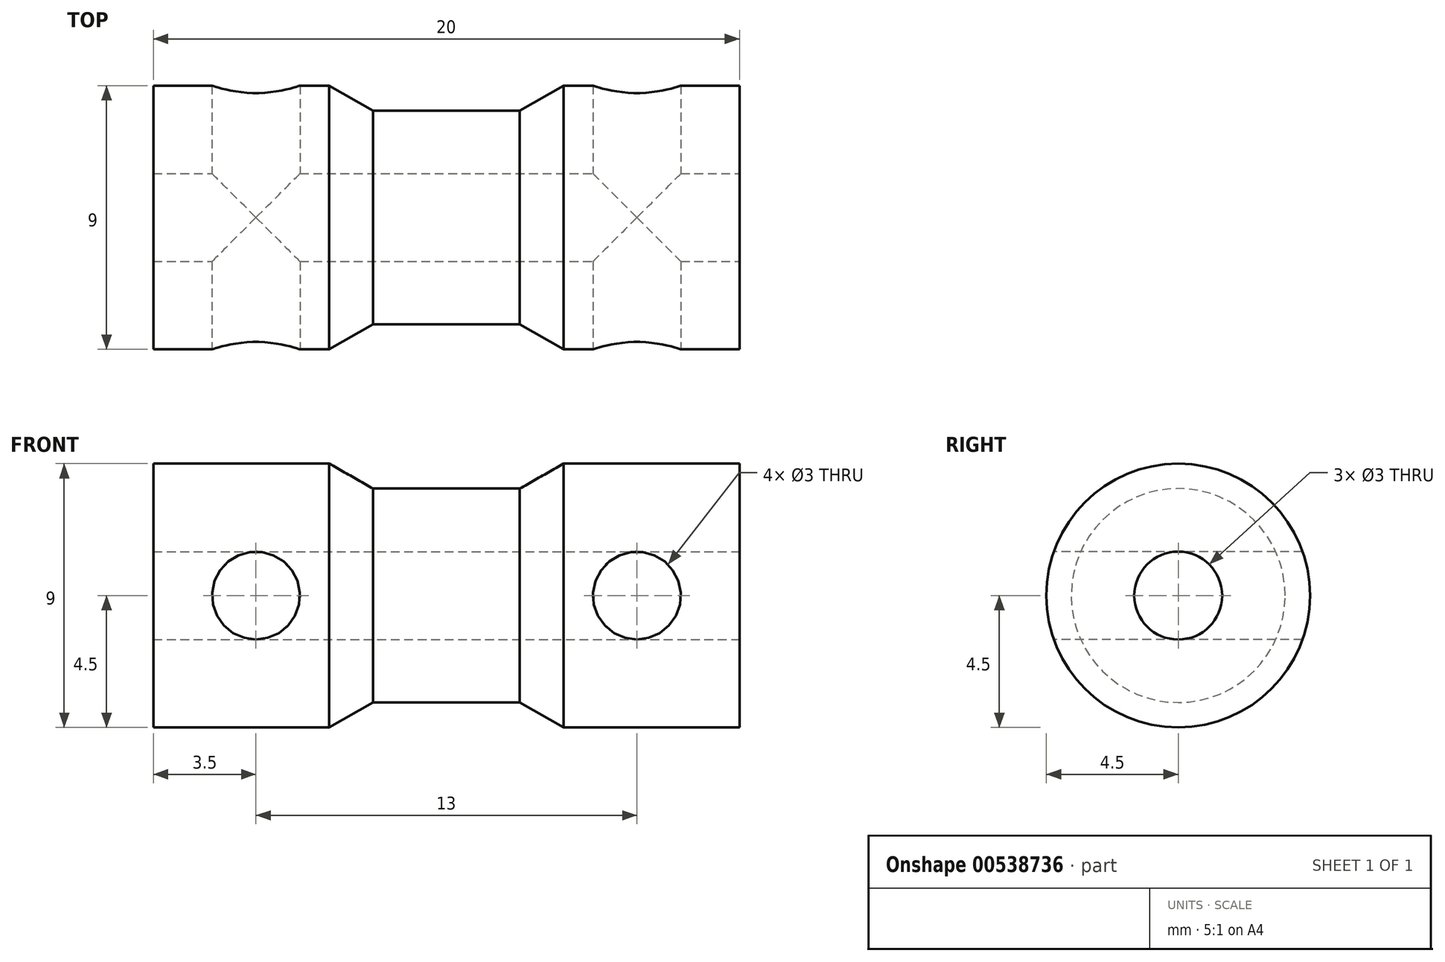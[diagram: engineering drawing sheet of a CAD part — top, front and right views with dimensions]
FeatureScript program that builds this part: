
annotation { "Feature Type Name" : "Feature", "Feature Type Description" : "" }
export const myFeature = defineFeature(function(context is Context, id is Id, definition is map)
    precondition{}
    {
        {
            var Q0;
            Q0=qCreatedBy(makeId("Front.planeOp"),FACE);
            var sketch = newSketch(context, id + "F0", { "sketchPlane" : qUnion([Q0])});
            skLineSegment(sketch, "E0", {"start": v(-10, 0) * mm, "end": v(-10, -4.5) * mm});
            skLineSegment(sketch, "E1", {"start": v(-10, -4.5) * mm, "end": v(-4, -4.5) * mm});
            skLineSegment(sketch, "E2", {"start": v(-2.5, -3.65) * mm, "end": v(0, -3.65) * mm});
            skLineSegment(sketch, "E3", {"start": v(-4, -4.5) * mm, "end": v(-2.5, -3.65) * mm});
            skLineSegment(sketch, "E4.MirrorCS", {"start": v(4, -4.5) * mm, "end": v(2.5, -3.65) * mm});
            skLineSegment(sketch, "E5.MirrorCS", {"start": v(10, -4.5) * mm, "end": v(4, -4.5) * mm});
            skLineSegment(sketch, "E6.MirrorCS", {"start": v(10, 0) * mm, "end": v(10, -4.5) * mm});
            skLineSegment(sketch, "E7.MirrorCS", {"start": v(2.5, -3.65) * mm, "end": v(0, -3.65) * mm});
            skLineSegment(sketch, "E8", {"start": v(-10, 0) * mm, "end": v(10, 0) * mm});
            skSolve(sketch);
        }
        {
            var Q0;
            Q0=makeQuery(id+"F0.imprint","IMPRINT",FACE,{"disambiguationData":[TD([[makeQuery(id+"F0.imprint","IMPRINT",EDGE,{"derivedFrom":sQuery(id+"F0.wireOp",EDGE,"E0")}),1.0]])]});
            var Q1;
            Q1=sQuery(id+"F0.wireOp",EDGE,"E8");
            revolve(context, id + "F1", {"surfaceOperationType" : NewSurfaceOperationType.NEW, "entities" : qUnion([Q0]), "axis" : qUnion([Q1]), "revolveType" : RevolveType.FULL});
        }
        {
            var Q0;
            Q0=qCreatedBy(makeId("Front.planeOp"),FACE);
            var sketch = newSketch(context, id + "F2", { "sketchPlane" : qUnion([Q0])});
            skCircle(sketch, "E9", {"center": v(-6.5, 0) * mm, "radius": 1.5 * mm});
            skCircle(sketch, "E10.MirrorC", {"center": v(6.5, 0) * mm, "radius": 1.5 * mm});
            skSolve(sketch);
        }
        {
            var Q0;
            Q0 = qSketchRegion(id + "F2", true);
            extrude(context, id + "F3", {"entities" : qUnion([Q0]), "operationType" : NewBodyOperationType.REMOVE, "endBound" : BoundingType.THROUGH_ALL, "oppositeDirection" : true, "depth" : 25 * mm, "offsetDistance" : 25 * mm, "hasSecondDirection" : true, "secondDirectionBound" : SecondDirectionBoundingType.THROUGH_ALL, "secondDirectionOppositeDirection" : false, "secondDirectionDepth" : 25 * mm});
        }
        {
            var Q0;
            Q0=makeQuery(id+"F1.opRevolve","SWEPT_FACE",FACE,{"disambiguationData":[OSD([sQuery(id+"F0.wireOp",EDGE,"E6.MirrorCS")])]});
            var sketch = newSketch(context, id + "F4", { "sketchPlane" : qUnion([Q0])});
            skCircle(sketch, "E11", {"center": v(0, 0) * mm, "radius": 1.5 * mm});
            skSolve(sketch);
        }
        {
            var Q0;
            Q0=makeQuery(id+"F4.imprint","IMPRINT",FACE,{"disambiguationData":[TD([[makeQuery(id+"F4.imprint","IMPRINT",EDGE,{"derivedFrom":sQuery(id+"F4.wireOp",EDGE,"E11")}),1.0]])]});
            extrude(context, id + "F5", {"entities" : qUnion([Q0]), "operationType" : NewBodyOperationType.REMOVE, "oppositeDirection" : true, "depth" : 25 * mm, "offsetDistance" : 25 * mm, "hasSecondDirection" : true, "secondDirectionOppositeDirection" : false, "secondDirectionDepth" : 25 * mm});
        }
    });
